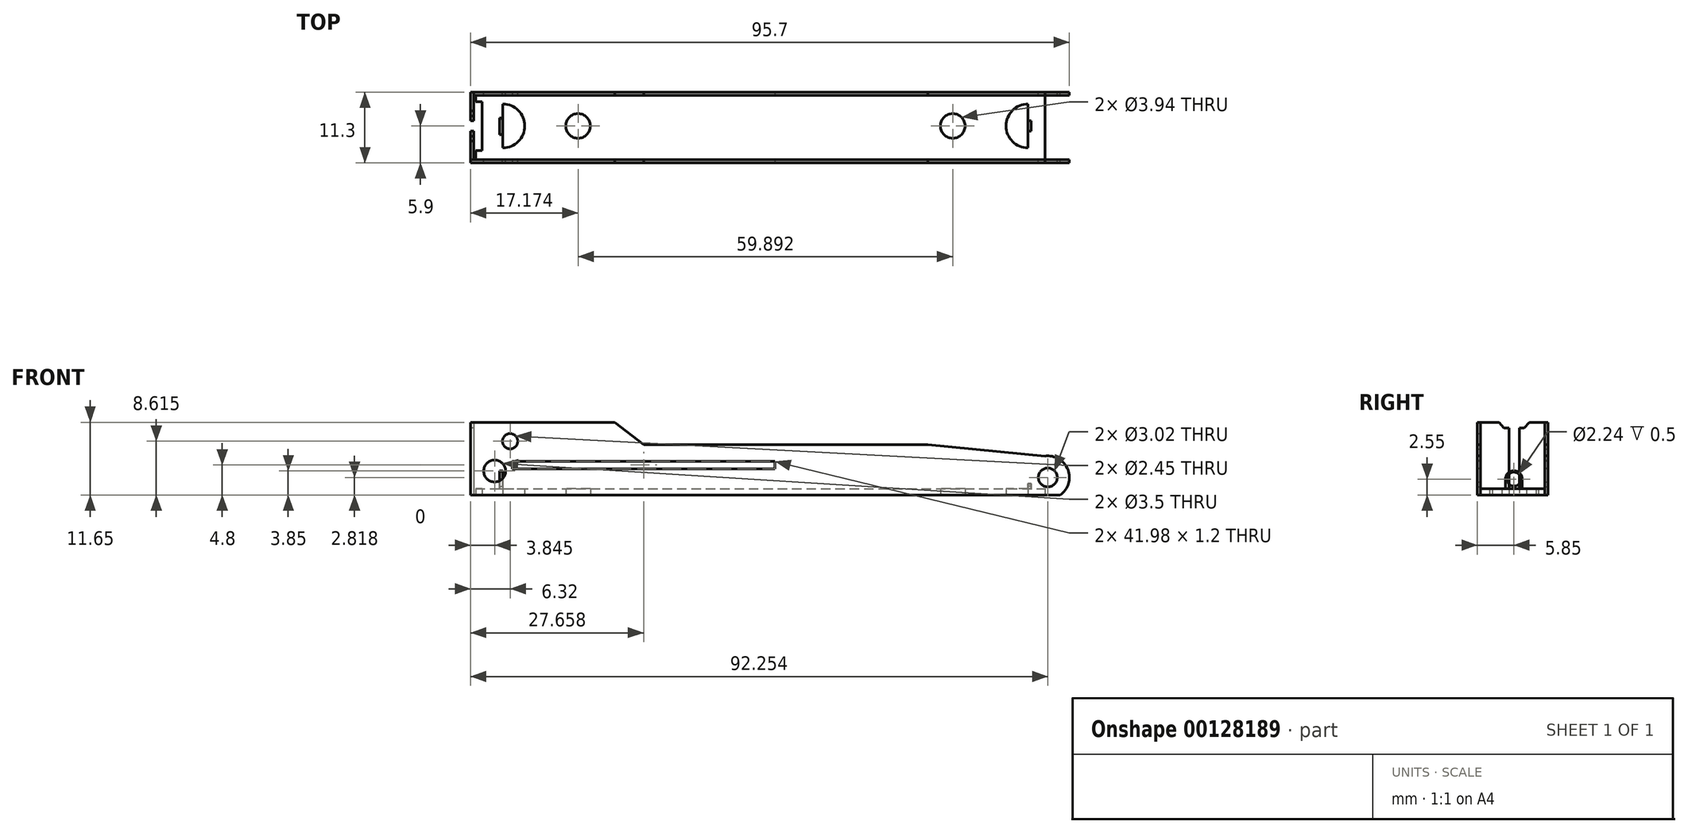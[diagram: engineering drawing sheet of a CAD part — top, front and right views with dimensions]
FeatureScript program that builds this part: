
annotation { "Feature Type Name" : "Feature", "Feature Type Description" : "" }
export const myFeature = defineFeature(function(context is Context, id is Id, definition is map)
    precondition{}
    {
        {
            var Q0;
            Q0=qCreatedBy(makeId("Front.planeOp"),FACE);
            var sketch = newSketch(context, id + "F0", { "sketchPlane" : qUnion([Q0])});
            skLineSegment(sketch, "E0", {"start": v(-47.12, 11.6) * mm, "end": v(-47.12, 0) * mm});
            skLineSegment(sketch, "E1", {"start": v(-47.12, 0) * mm, "end": v(47.12, 0) * mm});
            skLineSegment(sketch, "E2", {"start": v(-47.12, 11.6) * mm, "end": v(-24.1, 11.6) * mm});
            skLineSegment(sketch, "E3", {"start": v(-24.1, 11.6) * mm, "end": v(-19.42, 8.08) * mm});
            skLineSegment(sketch, "E4", {"start": v(-19.42, 8.08) * mm, "end": v(25.99, 8.08) * mm});
            skLineSegment(sketch, "E5", {"start": v(25.99, 8.08) * mm, "end": v(44.68, 6.24) * mm});
            skCircle(sketch, "E6", {"center": v(45.13, 2.82) * mm, "radius": 1.51 * mm});
            skArc(sketch, "E7", {"start": v(47.12, 0) * mm, "mid": v(48.35, 4.08) * mm, "end": v(44.68, 6.24) * mm});
            skCircle(sketch, "E8", {"center": v(-40.8, 8.62) * mm, "radius": 1.23 * mm});
            skCircle(sketch, "E9", {"center": v(-43.27, 3.85) * mm, "radius": 1.75 * mm});
            skLineSegment(sketch, "E10", {"start": v(44.68, 6.24) * mm, "end": v(44.68, 0) * mm, "construction": true});
            skSolve(sketch);
        }
        {
            var Q0;
            Q0=qCreatedBy(makeId("Front.planeOp"),FACE);
            cPlane(context, id + "F1", {"entities" : qUnion([Q0]), "cplaneType" : CPlaneType.OFFSET, "offset" : 10.8 * mm, "oppositeDirection" : true, "width" : 150 * mm, "height" : 150 * mm});
        }
        {
            var Q0;
            Q0=qCreatedBy(id+"F1.planeOp",FACE);
            var sketch = newSketch(context, id + "F2", { "sketchPlane" : qUnion([Q0])});
            skLineSegment(sketch, "E11.0.0", {"start": v(-24.1, 11.6) * mm, "end": v(-47.12, 11.6) * mm});
            skLineSegment(sketch, "E11.0.1", {"start": v(-47.12, 11.6) * mm, "end": v(-47.12, 0) * mm});
            skLineSegment(sketch, "E11.0.2", {"start": v(-47.12, 0) * mm, "end": v(47.12, 0) * mm});
            skArc(sketch, "E11.0.3", {"start": v(47.12, 0) * mm, "mid": v(48.35, 4.08) * mm, "end": v(44.68, 6.24) * mm});
            skLineSegment(sketch, "E11.0.4", {"start": v(44.68, 6.24) * mm, "end": v(25.99, 8.08) * mm});
            skLineSegment(sketch, "E11.0.5", {"start": v(25.99, 8.08) * mm, "end": v(-19.42, 8.08) * mm});
            skLineSegment(sketch, "E11.0.6", {"start": v(-19.42, 8.08) * mm, "end": v(-24.1, 11.6) * mm});
            skCircle(sketch, "E12.0", {"center": v(-43.27, 3.85) * mm, "radius": 1.75 * mm});
            skCircle(sketch, "E12.1", {"center": v(-40.8, 8.62) * mm, "radius": 1.23 * mm});
            skCircle(sketch, "E12.2", {"center": v(45.13, 2.82) * mm, "radius": 1.51 * mm});
            skSolve(sketch);
        }
        {
            var Q0;
            Q0=qCreatedBy(makeId("Right.planeOp"),FACE);
            cPlane(context, id + "F3", {"entities" : qUnion([Q0]), "cplaneType" : CPlaneType.OFFSET, "offset" : 44.68 * mm, "width" : 150 * mm, "height" : 150 * mm});
        }
        {
            var Q0;
            Q0=qCreatedBy(makeId("Right.planeOp"),FACE);
            cPlane(context, id + "F4", {"entities" : qUnion([Q0]), "cplaneType" : CPlaneType.OFFSET, "offset" : 47.12 * mm, "oppositeDirection" : true, "width" : 150 * mm, "height" : 150 * mm});
        }
        {
            var Q0;
            Q0=qCreatedBy(id+"F3.planeOp",FACE);
            var sketch = newSketch(context, id + "F5", { "sketchPlane" : qUnion([Q0])});
            skLineSegment(sketch, "E13", {"start": v(0, 0) * mm, "end": v(10.8, 0) * mm});
            skSolve(sketch);
        }
        {
            var Q0;
            Q0=qCreatedBy(id+"F4.planeOp",FACE);
            var sketch = newSketch(context, id + "F6", { "sketchPlane" : qUnion([Q0])});
            skLineSegment(sketch, "E14", {"start": v(10.8, 11.65) * mm, "end": v(0, 11.65) * mm});
            skLineSegment(sketch, "E15", {"start": v(0, 11.65) * mm, "end": v(0, 0) * mm});
            skLineSegment(sketch, "E16", {"start": v(0, 0) * mm, "end": v(10.8, 0) * mm});
            skLineSegment(sketch, "E17", {"start": v(10.8, 0) * mm, "end": v(10.8, 11.65) * mm});
            skLineSegment(sketch, "E18", {"start": v(0, 11.65) * mm, "end": v(3, 11.65) * mm});
            skLineSegment(sketch, "E19", {"start": v(3, 11.65) * mm, "end": v(3.78, 10.72) * mm});
            skLineSegment(sketch, "E20", {"start": v(7.02, 10.72) * mm, "end": v(7.8, 11.65) * mm});
            skLineSegment(sketch, "E21", {"start": v(7.02, 10.72) * mm, "end": v(6.22, 10.72) * mm});
            skLineSegment(sketch, "E22", {"start": v(3.78, 10.72) * mm, "end": v(4.58, 10.72) * mm});
            skLineSegment(sketch, "E23", {"start": v(6.22, 10.72) * mm, "end": v(6.22, 0) * mm});
            skLineSegment(sketch, "E24", {"start": v(4.58, 10.72) * mm, "end": v(4.58, 0) * mm});
            skLineSegment(sketch, "E25", {"start": v(4.58, 0) * mm, "end": v(6.22, 0) * mm});
            skSolve(sketch);
        }
        {
            var Q0;
            Q0=qCreatedBy(makeId("Top.planeOp"),FACE);
            var sketch = newSketch(context, id + "F7", { "sketchPlane" : qUnion([Q0])});
            skLineSegment(sketch, "E26.0", {"start": v(-47.12, 0) * mm, "end": v(-24.1, 0) * mm});
            skLineSegment(sketch, "E26.1", {"start": v(-19.42, 0) * mm, "end": v(25.99, 0) * mm});
            skLineSegment(sketch, "E26.2", {"start": v(-24.1, 0) * mm, "end": v(-19.42, 0) * mm});
            skLineSegment(sketch, "E26.3", {"start": v(25.99, 0) * mm, "end": v(44.68, 0) * mm});
            skLineSegment(sketch, "E26.4", {"start": v(44.68, 10.8) * mm, "end": v(25.99, 10.8) * mm});
            skLineSegment(sketch, "E26.5", {"start": v(25.99, 10.8) * mm, "end": v(-19.42, 10.8) * mm});
            skLineSegment(sketch, "E26.7", {"start": v(-47.12, 10.8) * mm, "end": v(-47.12, 0) * mm});
            skLineSegment(sketch, "E26.8", {"start": v(44.68, 0) * mm, "end": v(44.68, 10.8) * mm});
            skLineSegment(sketch, "E27", {"start": v(41.98, 1.9) * mm, "end": v(41.98, 8.91) * mm});
            skArc(sketch, "E28", {"start": v(41.98, 8.91) * mm, "mid": v(38.47, 5.4) * mm, "end": v(41.98, 1.9) * mm});
            skCircle(sketch, "E29", {"center": v(29.95, 5.4) * mm, "radius": 1.97 * mm});
            skArc(sketch, "E30.MirrorCS", {"start": v(-41.98, 8.91) * mm, "mid": v(-38.47, 5.4) * mm, "end": v(-41.98, 1.9) * mm});
            skLineSegment(sketch, "E31.MirrorCS", {"start": v(-41.98, 1.9) * mm, "end": v(-41.98, 8.91) * mm});
            skCircle(sketch, "E32.MirrorC", {"center": v(-29.95, 5.4) * mm, "radius": 1.97 * mm});
            skLineSegment(sketch, "E33", {"start": v(-46.32, 0) * mm, "end": v(-46.32, 1.5) * mm});
            skLineSegment(sketch, "E34", {"start": v(-46.32, 1.5) * mm, "end": v(-45.26, 1.5) * mm});
            skLineSegment(sketch, "E35", {"start": v(-45.26, 1.5) * mm, "end": v(-45.26, 9.3) * mm});
            skLineSegment(sketch, "E36", {"start": v(-45.26, 9.3) * mm, "end": v(-46.33, 9.3) * mm});
            skLineSegment(sketch, "E37", {"start": v(-46.33, 9.3) * mm, "end": v(-46.33, 10.8) * mm});
            skLineSegment(sketch, "E38", {"start": v(-47.12, 10.8) * mm, "end": v(-47.12, 5.95) * mm});
            skLineSegment(sketch, "E39", {"start": v(-47.12, 0) * mm, "end": v(-47.12, 4.45) * mm});
            skLineSegment(sketch, "E40", {"start": v(-47.12, 10.8) * mm, "end": v(44.68, 10.8) * mm});
            skSolve(sketch);
        }
        {
            var Q0;
            Q0=makeQuery(id+"F0.imprint","IMPRINT",FACE,{"disambiguationData":[TD([[makeQuery(id+"F0.imprint","IMPRINT",EDGE,{"derivedFrom":sQuery(id+"F0.wireOp",EDGE,"E0")}),1.0]])]});
            var Q1;
            Q1=makeQuery(id+"F2.imprint","IMPRINT",FACE,{"disambiguationData":[TD([[makeQuery(id+"F2.imprint","IMPRINT",EDGE,{"derivedFrom":sQuery(id+"F2.wireOp",EDGE,"E11.0.0")}),1.0]])]});
            extrude(context, id + "F8", {"entities" : qUnion([Q0, Q1]), "depth" : 0.5 * mm});
        }
        {
            var Q0;
            Q0=makeQuery(id+"F6.imprint","IMPRINT",FACE,{"disambiguationData":[TD([[makeQuery(id+"F6.imprint","IMPRINT",EDGE,{"derivedFrom":sQuery(id+"F6.wireOp",EDGE,"E14")}),1.0]])]});
            var Q1;
            {var subQ1=sQuery(id+"F6.wireOp",EDGE,"E15");Q1=makeQuery(id+"F6.imprint","IMPRINT",FACE,{"disambiguationData":[TD([[makeQuery(id+"F6.imprint","IMPRINT",EDGE,{"derivedFrom":subQ1}),1.0]])]});}
            extrude(context, id + "F9", {"entities" : qUnion([Q0, Q1]), "operationType" : NewBodyOperationType.ADD, "depth" : 0.5 * mm});
        }
        {
            var Q0;
            Q0=makeQuery(id+"F7.imprint","IMPRINT",FACE,{"disambiguationData":[TD([[makeQuery(id+"F7.imprint","IMPRINT",EDGE,{"derivedFrom":sQuery(id+"F7.wireOp",EDGE,"E26.0")}),1.0]])]});
            extrude(context, id + "F10", {"entities" : qUnion([Q0]), "operationType" : NewBodyOperationType.ADD, "depth" : 0.5 * mm});
        }
        {
            var Q0;
            {var subQ6=sQuery(id+"F7.wireOp",EDGE,"E26.1");Q0=makeQuery(id+"F7.imprint","IMPRINT",FACE,{"disambiguationData":[TD([[makeQuery(id+"F7.imprint","IMPRINT",EDGE,{"derivedFrom":subQ6}),1.0]])]});}
            extrude(context, id + "F11", {"entities" : qUnion([Q0]), "operationType" : NewBodyOperationType.ADD, "depth" : 1 * mm});
        }
        {
            var Q0;
            {var subQ1=sQuery(id+"F6.wireOp",EDGE,"E15");Q0=makeQuery(id+"F6.imprint","IMPRINT",FACE,{"disambiguationData":[TD([[makeQuery(id+"F6.imprint","IMPRINT",EDGE,{"derivedFrom":subQ1}),1.0]])]});}
            extrude(context, id + "F12", {"entities" : qUnion([Q0]), "operationType" : NewBodyOperationType.ADD, "depth" : 0.5 * mm});
        }
        {
            var Q0;
            Q0=makeQuery(id+"F10.opExtrude","CAP_FACE",FACE,{"disambiguationData":[OSD([sQuery(id+"F7.wireOp",EDGE,"E26.0"),sQuery(id+"F7.wireOp",EDGE,"E26.7"),sQuery(id+"F7.wireOp",EDGE,"E33"),sQuery(id+"F7.wireOp",EDGE,"E34"),sQuery(id+"F7.wireOp",EDGE,"E35"),sQuery(id+"F7.wireOp",EDGE,"E36"),sQuery(id+"F7.wireOp",EDGE,"E37"),sQuery(id+"F7.wireOp",EDGE,"E38"),sQuery(id+"F7.wireOp",EDGE,"E39"),sQuery(id+"F7.wireOp",EDGE,"E40")])],"isStart":false});
            extrude(context, id + "F13", {"entities" : qUnion([Q0]), "operationType" : NewBodyOperationType.REMOVE, "oppositeDirection" : true, "depth" : 25 * mm});
        }
        {
            var Q0;
            Q0=makeQuery(id+"F11.opExtrude","SWEPT_FACE",FACE,{"disambiguationData":[OSD([sQuery(id+"F7.wireOp",EDGE,"E31.MirrorCS")])]});
            var sketch = newSketch(context, id + "F14", { "sketchPlane" : qUnion([Q0])});
            skLineSegment(sketch, "E41.0", {"start": v(0, 1) * mm, "end": v(10.3, 1) * mm});
            skLineSegment(sketch, "E42.0", {"start": v(4.58, 10.72) * mm, "end": v(4.58, 0) * mm});
            skLineSegment(sketch, "E42.1", {"start": v(6.22, 10.72) * mm, "end": v(6.22, 0) * mm});
            skCircle(sketch, "E43", {"center": v(5.35, 2.55) * mm, "radius": 1.12 * mm});
            skLineSegment(sketch, "E44", {"start": v(4, 1) * mm, "end": v(6.7, 1) * mm});
            skLineSegment(sketch, "E45", {"start": v(4, 1) * mm, "end": v(4, 2.55) * mm});
            skLineSegment(sketch, "E46", {"start": v(6.7, 2.55) * mm, "end": v(6.7, 1) * mm});
            skArc(sketch, "E47", {"start": v(6.7, 2.55) * mm, "mid": v(5.35, 3.9) * mm, "end": v(4, 2.55) * mm});
            skLineSegment(sketch, "E48.0", {"start": v(0, 0) * mm, "end": v(0, 6.27) * mm});
            skLineSegment(sketch, "E48.1", {"start": v(10.3, 0) * mm, "end": v(10.3, 6.27) * mm});
            skSolve(sketch);
        }
        {
            var Q0;
            Q0=makeQuery(id+"F11.opExtrude","SWEPT_FACE",FACE,{"disambiguationData":[OSD([sQuery(id+"F7.wireOp",EDGE,"E27")])]});
            var sketch = newSketch(context, id + "F15", { "sketchPlane" : qUnion([Q0])});
            skArc(sketch, "E49.0.0", {"start": v(-6.22, 1.84) * mm, "mid": v(-5.42, 1.43) * mm, "end": v(-4.58, 1.74) * mm});
            skLineSegment(sketch, "E49.0.1", {"start": v(-4.58, 1.74) * mm, "end": v(-4.58, 1) * mm});
            skLineSegment(sketch, "E49.0.2", {"start": v(-4.58, 1) * mm, "end": v(-6.22, 1) * mm});
            skLineSegment(sketch, "E49.0.3", {"start": v(-6.22, 1) * mm, "end": v(-6.22, 1.84) * mm});
            skArc(sketch, "E49.1.0", {"start": v(-6.22, 3.58) * mm, "mid": v(-5.41, 3.9) * mm, "end": v(-4.58, 3.66) * mm});
            skLineSegment(sketch, "E49.1.1", {"start": v(-4.58, 3.66) * mm, "end": v(-4.58, 3.36) * mm});
            skArc(sketch, "E49.1.2", {"start": v(-4.58, 3.36) * mm, "mid": v(-5.42, 3.67) * mm, "end": v(-6.22, 3.26) * mm});
            skLineSegment(sketch, "E49.1.3", {"start": v(-6.22, 3.26) * mm, "end": v(-6.22, 3.58) * mm});
            skArc(sketch, "E49.2.0", {"start": v(-6.7, 2.55) * mm, "mid": v(-6.57, 3.12) * mm, "end": v(-6.22, 3.58) * mm});
            skLineSegment(sketch, "E49.2.1", {"start": v(-6.22, 3.58) * mm, "end": v(-6.22, 3.26) * mm});
            skArc(sketch, "E49.2.2", {"start": v(-6.22, 3.26) * mm, "mid": v(-6.47, 2.55) * mm, "end": v(-6.22, 1.84) * mm});
            skLineSegment(sketch, "E49.2.3", {"start": v(-6.22, 1.84) * mm, "end": v(-6.22, 1) * mm});
            skLineSegment(sketch, "E49.2.4", {"start": v(-6.22, 1) * mm, "end": v(-6.7, 1) * mm});
            skLineSegment(sketch, "E49.2.5", {"start": v(-6.7, 1) * mm, "end": v(-6.7, 2.55) * mm});
            skLineSegment(sketch, "E49.3.0", {"start": v(-4.58, 3.36) * mm, "end": v(-4.58, 3.66) * mm});
            skArc(sketch, "E49.3.1", {"start": v(-4.58, 3.66) * mm, "mid": v(-4.15, 3.18) * mm, "end": v(-4, 2.55) * mm});
            skLineSegment(sketch, "E49.3.2", {"start": v(-4, 2.55) * mm, "end": v(-4, 1) * mm});
            skLineSegment(sketch, "E49.3.3", {"start": v(-4, 1) * mm, "end": v(-4.58, 1) * mm});
            skLineSegment(sketch, "E49.3.4", {"start": v(-4.58, 1) * mm, "end": v(-4.58, 1.74) * mm});
            skArc(sketch, "E49.3.5", {"start": v(-4.58, 1.74) * mm, "mid": v(-4.23, 2.55) * mm, "end": v(-4.58, 3.36) * mm});
            skSolve(sketch);
        }
        {
            var Q0;
            {var subQ0=sQuery(id+"F14.wireOp",EDGE,"E45");Q0=makeQuery(id+"F14.imprint","IMPRINT",FACE,{"disambiguationData":[TD([[makeQuery(id+"F14.imprint","IMPRINT",EDGE,{"derivedFrom":subQ0}),-1.0]])]});}
            var Q1;
            {var subQ0=sQuery(id+"F14.wireOp",EDGE,"E47");var subQ1=sQuery(id+"F14.wireOp",EDGE,"E42.0");var subQ2=makeQuery(id+"F14.imprint","INTERSECT",VERTEX,{"derivedFrom":[subQ1,subQ0]});Q1=makeQuery(id+"F14.imprint","IMPRINT",FACE,{"disambiguationData":[TD([[makeQuery(id+"F14.imprint","IMPRINT",EDGE,{"disambiguationData":[TD([[subQ2,-1.0]])],"derivedFrom":subQ1}),1.0]])]});}
            var Q2;
            {var subQ0=sQuery(id+"F14.wireOp",EDGE,"E43");var subQ1=sQuery(id+"F14.wireOp",EDGE,"E42.0");var subQ2=makeQuery(id+"F14.imprint","INTERSECT",VERTEX,{"disambiguationData":[OD(1.0)],"derivedFrom":[subQ1,subQ0]});Q2=makeQuery(id+"F14.imprint","IMPRINT",FACE,{"disambiguationData":[TD([[makeQuery(id+"F14.imprint","IMPRINT",EDGE,{"disambiguationData":[TD([[subQ2,-1.0]])],"derivedFrom":subQ1}),1.0]])]});}
            var Q3;
            {var subQ0=sQuery(id+"F14.wireOp",EDGE,"E46");Q3=makeQuery(id+"F14.imprint","IMPRINT",FACE,{"disambiguationData":[TD([[makeQuery(id+"F14.imprint","IMPRINT",EDGE,{"derivedFrom":subQ0}),-1.0]])]});}
            extrude(context, id + "F16", {"entities" : qUnion([Q0, Q1, Q2, Q3]), "operationType" : NewBodyOperationType.ADD, "oppositeDirection" : true, "depth" : 0.5 * mm});
        }
        {
            var Q0;
            Q0=makeQuery(id+"F15.imprint","IMPRINT",FACE,{"disambiguationData":[TD([[makeQuery(id+"F15.imprint","IMPRINT",EDGE,{"derivedFrom":sQuery(id+"F15.wireOp",EDGE,"E49.3.0")}),-1.0]])]});
            var Q1;
            Q1=makeQuery(id+"F15.imprint","IMPRINT",FACE,{"disambiguationData":[TD([[makeQuery(id+"F15.imprint","IMPRINT",EDGE,{"derivedFrom":sQuery(id+"F15.wireOp",EDGE,"E49.1.0")}),-1.0]])]});
            var Q2;
            Q2=makeQuery(id+"F15.imprint","IMPRINT",FACE,{"disambiguationData":[TD([[makeQuery(id+"F15.imprint","IMPRINT",EDGE,{"derivedFrom":sQuery(id+"F15.wireOp",EDGE,"E49.2.0")}),-1.0]])]});
            var Q3;
            Q3=makeQuery(id+"F15.imprint","IMPRINT",FACE,{"disambiguationData":[TD([[makeQuery(id+"F15.imprint","IMPRINT",EDGE,{"derivedFrom":sQuery(id+"F15.wireOp",EDGE,"E49.0.0")}),-1.0]])]});
            extrude(context, id + "F17", {"entities" : qUnion([Q0, Q1, Q2, Q3]), "operationType" : NewBodyOperationType.ADD, "oppositeDirection" : true, "depth" : 0.5 * mm});
        }
        {
            var Q0;
            Q0=makeQuery(id+"F8.opExtrude","CAP_FACE",FACE,{"disambiguationData":[OSD([sQuery(id+"F0.wireOp",EDGE,"E0"),sQuery(id+"F0.wireOp",EDGE,"E1"),sQuery(id+"F0.wireOp",EDGE,"E2"),sQuery(id+"F0.wireOp",EDGE,"E3"),sQuery(id+"F0.wireOp",EDGE,"E4"),sQuery(id+"F0.wireOp",EDGE,"E5"),sQuery(id+"F0.wireOp",EDGE,"E6"),sQuery(id+"F0.wireOp",EDGE,"E7"),sQuery(id+"F0.wireOp",EDGE,"E8"),sQuery(id+"F0.wireOp",EDGE,"E9")])],"isStart":false});
            var sketch = newSketch(context, id + "F18", { "sketchPlane" : qUnion([Q0])});
            skLineSegment(sketch, "E50.0", {"start": v(-47.12, 0) * mm, "end": v(-24.1, 0) * mm});
            skLineSegment(sketch, "E50.1", {"start": v(-24.1, 0) * mm, "end": v(-19.42, 0) * mm});
            skLineSegment(sketch, "E50.2", {"start": v(25.99, 0) * mm, "end": v(-19.42, 0) * mm});
            skLineSegment(sketch, "E50.3", {"start": v(44.68, 0) * mm, "end": v(25.99, 0) * mm});
            skPoint(sketch, "E51.0", {"position": v(41.98, 0) * mm});
            skPoint(sketch, "E52", {"position": v(1.53, 0) * mm});
            skLineSegment(sketch, "E53.bottom", {"start": v(-40.45, 5.4) * mm, "end": v(1.53, 5.4) * mm});
            skLineSegment(sketch, "E53.left", {"start": v(-40.45, 5.4) * mm, "end": v(-40.45, 4.2) * mm});
            skPoint(sketch, "E54", {"position": v(1.53, 4.2) * mm});
            skLineSegment(sketch, "E55", {"start": v(-40.45, 4.2) * mm, "end": v(1.53, 4.2) * mm});
            skLineSegment(sketch, "E56", {"start": v(1.53, 4.2) * mm, "end": v(1.53, 5.4) * mm});
            skSolve(sketch);
        }
        {
            var Q0;
            Q0 = qSketchRegion(id + "FcsCSCcG7qHl8KV_1", true);
            var Q1;
            Q1 = qSketchRegion(id + "F18", true);
            extrude(context, id + "F19", {"entities" : qUnion([Q0, Q1]), "operationType" : NewBodyOperationType.REMOVE, "endBound" : BoundingType.THROUGH_ALL, "oppositeDirection" : true, "depth" : 25 * mm});
        }
    });
